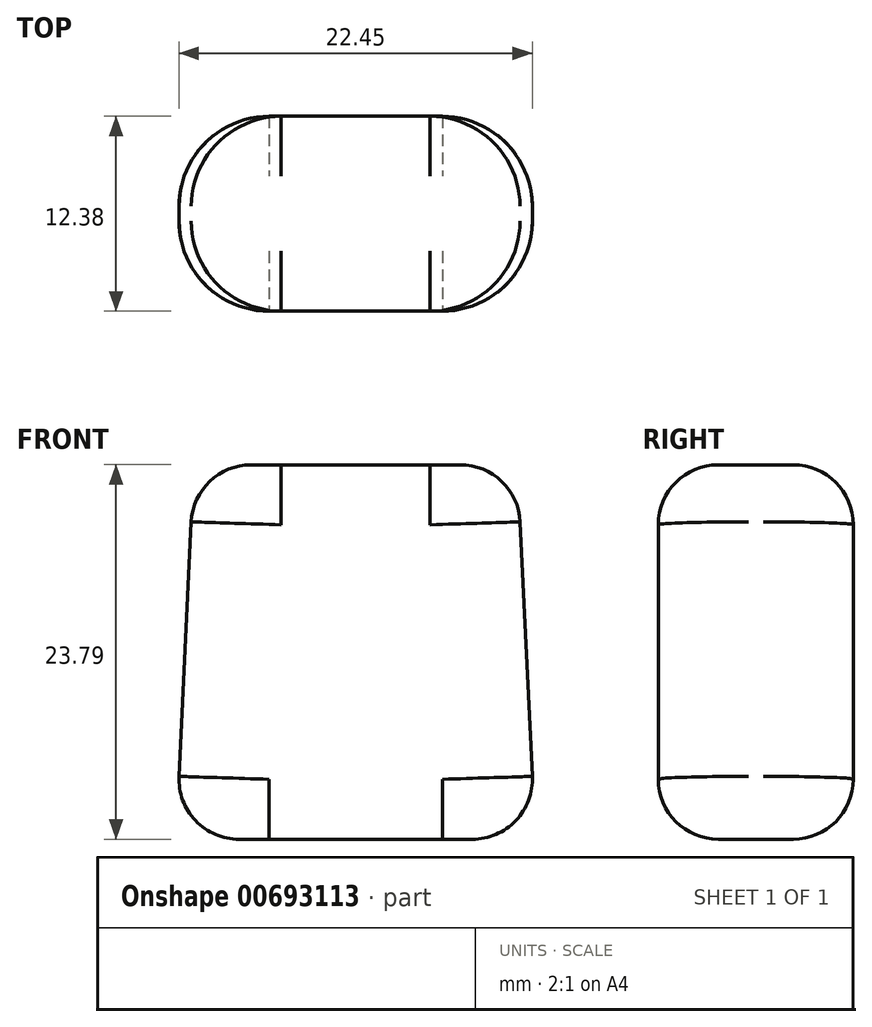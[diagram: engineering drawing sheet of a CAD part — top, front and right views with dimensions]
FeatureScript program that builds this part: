
annotation { "Feature Type Name" : "Feature", "Feature Type Description" : "" }
export const myFeature = defineFeature(function(context is Context, id is Id, definition is map)
    precondition{}
    {
        {
            var Q0;
            Q0=qCreatedBy(makeId("Front.planeOp"),FACE);
            var sketch = newSketch(context, id + "F0", { "sketchPlane" : qUnion([Q0])});
            skLineSegment(sketch, "E0", {"start": v(-15.36, 0) * mm, "end": v(15.06, 0) * mm});
            skLineSegment(sketch, "E1", {"start": v(-15.36, 0) * mm, "end": v(-13.85, 31.71) * mm});
            skLineSegment(sketch, "E2", {"start": v(-13.85, 31.71) * mm, "end": v(13.54, 31.71) * mm});
            skLineSegment(sketch, "E3", {"start": v(13.54, 31.71) * mm, "end": v(15.06, 0) * mm});
            skSolve(sketch);
        }
        {
            var Q0;
            Q0=makeQuery(id+"F0.imprint","IMPRINT",FACE,{"disambiguationData":[TD([[makeQuery(id+"F0.imprint","IMPRINT",EDGE,{"derivedFrom":sQuery(id+"F0.wireOp",EDGE,"E0")}),1.0]])]});
            extrude(context, id + "F1", {"entities" : qUnion([Q0]), "depth" : 16.5 * mm});
        }
        {
            var Q0;
            Q0=makeQuery(id+"F1.opExtrude","CAP_EDGE",EDGE,{"disambiguationData":[OSD([sQuery(id+"F0.wireOp",EDGE,"E1")])],"isStart":false});
            fillet(context, id + "F2", {"entities" : qUnion([Q0]), "radius" : 7.62 * mm, "tangentPropagation" : true, "allowEdgeOverflow" : false});
        }
        {
            var Q0;
            Q0=makeQuery(id+"F1.opExtrude","CAP_EDGE",EDGE,{"disambiguationData":[OSD([sQuery(id+"F0.wireOp",EDGE,"E3")])],"isStart":false});
            var Q1;
            Q1=makeQuery(id+"F1.opExtrude","CAP_EDGE",EDGE,{"disambiguationData":[OSD([sQuery(id+"F0.wireOp",EDGE,"E3")])],"isStart":true});
            var Q2;
            Q2=makeQuery(id+"F1.opExtrude","CAP_EDGE",EDGE,{"disambiguationData":[OSD([sQuery(id+"F0.wireOp",EDGE,"E1")])],"isStart":true});
            fillet(context, id + "F3", {"entities" : qUnion([Q0, Q1, Q2]), "radius" : 7.62 * mm, "tangentPropagation" : true, "allowEdgeOverflow" : false});
        }
        {
            var Q0;
            Q0=makeQuery(id+"F1.opExtrude","CAP_EDGE",EDGE,{"disambiguationData":[OSD([sQuery(id+"F0.wireOp",EDGE,"E0")])],"isStart":true});
            fillet(context, id + "F4", {"entities" : qUnion([Q0]), "radius" : 5.08 * mm, "tangentPropagation" : true, "allowEdgeOverflow" : false});
        }
        {
            var Q0;
            Q0=makeQuery(id+"F1.opExtrude","CAP_EDGE",EDGE,{"disambiguationData":[OSD([sQuery(id+"F0.wireOp",EDGE,"E2")])],"isStart":false});
            fillet(context, id + "F5", {"entities" : qUnion([Q0]), "radius" : 5.08 * mm, "tangentPropagation" : true, "allowEdgeOverflow" : false});
        }
        {
            var Q0;
            Q0=makeQuery(id+"F1.opExtrude","SWEPT_BODY",BODY,{"disambiguationData":[OSD([sQuery(id+"F0.wireOp",EDGE,"E0"),sQuery(id+"F0.wireOp",EDGE,"E1"),sQuery(id+"F0.wireOp",EDGE,"E2"),sQuery(id+"F0.wireOp",EDGE,"E3")])]});
            var Q1;
            Q1=qCreatedBy(makeId("Origin.pointOp"),VERTEX);
            transform(context, id + "F6", {"entities" : qUnion([Q0]), "transformType" : TransformType.SCALE_UNIFORMLY, "scale" : 0.75, "scalePoint" : qUnion([Q1]), "makeCopy" : false});
        }
    });
